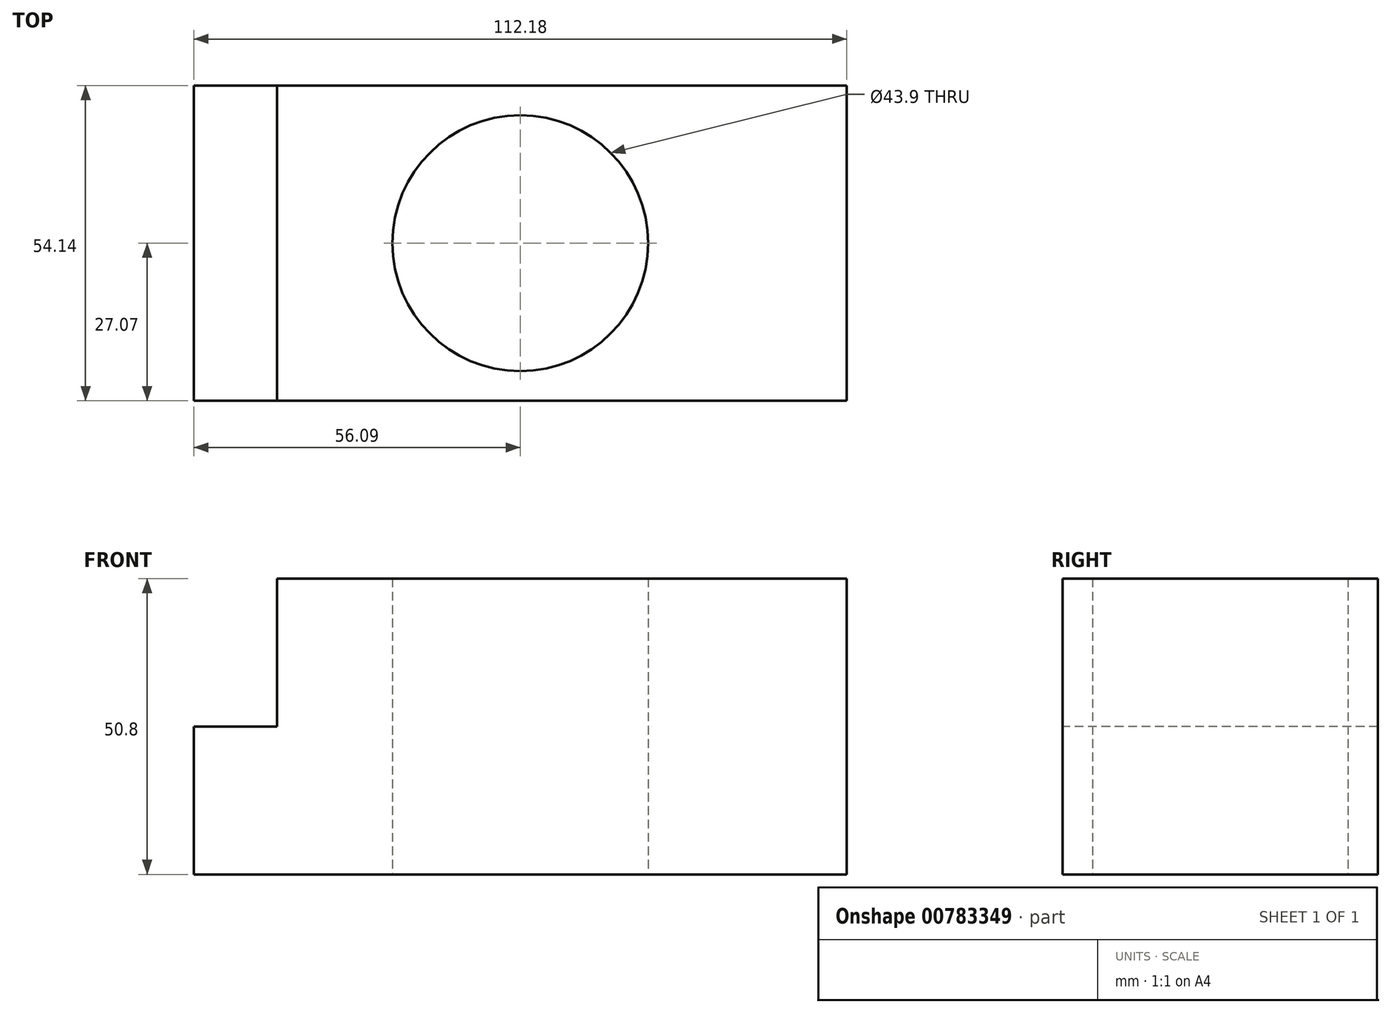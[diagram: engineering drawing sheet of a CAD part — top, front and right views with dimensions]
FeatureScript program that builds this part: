
annotation { "Feature Type Name" : "Feature", "Feature Type Description" : "" }
export const myFeature = defineFeature(function(context is Context, id is Id, definition is map)
    precondition{}
    {
        {
            var Q0;
            Q0=qCreatedBy(makeId("Top.planeOp"),FACE);
            var sketch = newSketch(context, id + "F0", { "sketchPlane" : qUnion([Q0])});
            skLineSegment(sketch, "E0.bottom", {"start": v(56.1, 27.07) * mm, "end": v(-56.1, 27.07) * mm});
            skLineSegment(sketch, "E0.top", {"start": v(56.1, -27.07) * mm, "end": v(-56.1, -27.07) * mm});
            skLineSegment(sketch, "E0.left", {"start": v(56.1, 27.07) * mm, "end": v(56.1, -27.07) * mm});
            skLineSegment(sketch, "E0.right", {"start": v(-56.1, 27.07) * mm, "end": v(-56.1, -27.07) * mm});
            skPoint(sketch, "E0.middle", {"position": v(0, 0) * mm});
            skCircle(sketch, "E1", {"center": v(0, 0) * mm, "radius": 21.95 * mm});
            skLineSegment(sketch, "E2.bottom", {"start": v(-49.42, 27.07) * mm, "end": v(-42.37, 27.07) * mm});
            skLineSegment(sketch, "E2.top", {"start": v(-49.42, -27.07) * mm, "end": v(-42.37, -27.07) * mm});
            skLineSegment(sketch, "E2.left", {"start": v(-49.42, 27.07) * mm, "end": v(-49.42, -27.07) * mm});
            skLineSegment(sketch, "E2.right", {"start": v(-42.37, 27.07) * mm, "end": v(-42.37, -27.07) * mm});
            skSolve(sketch);
        }
        {
            var Q0;
            {var subQ0=sQuery(id+"F0.wireOp",EDGE,"E0.left");Q0=makeQuery(id+"F0.imprint","IMPRINT",FACE,{"disambiguationData":[TD([[makeQuery(id+"F0.imprint","IMPRINT",EDGE,{"derivedFrom":subQ0}),-1.0]])]});}
            var Q1;
            {var subQ0=sQuery(id+"F0.wireOp",EDGE,"E2.left");Q1=makeQuery(id+"F0.imprint","IMPRINT",FACE,{"disambiguationData":[TD([[makeQuery(id+"F0.imprint","IMPRINT",EDGE,{"derivedFrom":subQ0}),1.0]])]});}
            var Q2;
            {var subQ0=sQuery(id+"F0.wireOp",EDGE,"E0.right");Q2=makeQuery(id+"F0.imprint","IMPRINT",FACE,{"disambiguationData":[TD([[makeQuery(id+"F0.imprint","IMPRINT",EDGE,{"derivedFrom":subQ0}),1.0]])]});}
            extrude(context, id + "F1", {"entities" : qUnion([Q0, Q1, Q2]), "depth" : 25.4 * mm, "offsetDistance" : 25.4 * mm});
        }
        {
            var Q0;
            Q0=makeQuery(id+"F1.opExtrude","CAP_FACE",FACE,{"disambiguationData":[OSD([sQuery(id+"F0.wireOp",EDGE,"E0.bottom"),sQuery(id+"F0.wireOp",EDGE,"E0.top"),sQuery(id+"F0.wireOp",EDGE,"E0.left"),sQuery(id+"F0.wireOp",EDGE,"E0.right"),sQuery(id+"F0.wireOp",EDGE,"E1")])],"isStart":false});
            var sketch = newSketch(context, id + "F2", { "sketchPlane" : qUnion([Q0])});
            skLineSegment(sketch, "E3.bottom", {"start": v(-41.81, 27.07) * mm, "end": v(-39.03, 27.07) * mm});
            skLineSegment(sketch, "E3.top", {"start": v(-41.81, -27.07) * mm, "end": v(-39.03, -27.07) * mm});
            skLineSegment(sketch, "E3.left", {"start": v(-41.81, 27.07) * mm, "end": v(-41.81, -27.07) * mm});
            skLineSegment(sketch, "E3.right", {"start": v(-39.03, 27.07) * mm, "end": v(-39.03, -27.07) * mm});
            skSolve(sketch);
        }
        {
            var Q0;
            Q0 = qSketchRegion(id + "F2", true);
            var Q1;
            {var subQ2=sQuery(id+"F2.wireOp",EDGE,"E3.right");Q1=makeQuery(id+"F2.imprint","IMPRINT",FACE,{"disambiguationData":[TD([[makeQuery(id+"F2.imprint","IMPRINT",EDGE,{"derivedFrom":subQ2}),1.0]])]});}
            extrude(context, id + "F3", {"entities" : qUnion([Q0, Q1]), "operationType" : NewBodyOperationType.ADD, "depth" : 25.4 * mm, "offsetDistance" : 25.4 * mm});
        }
    });
